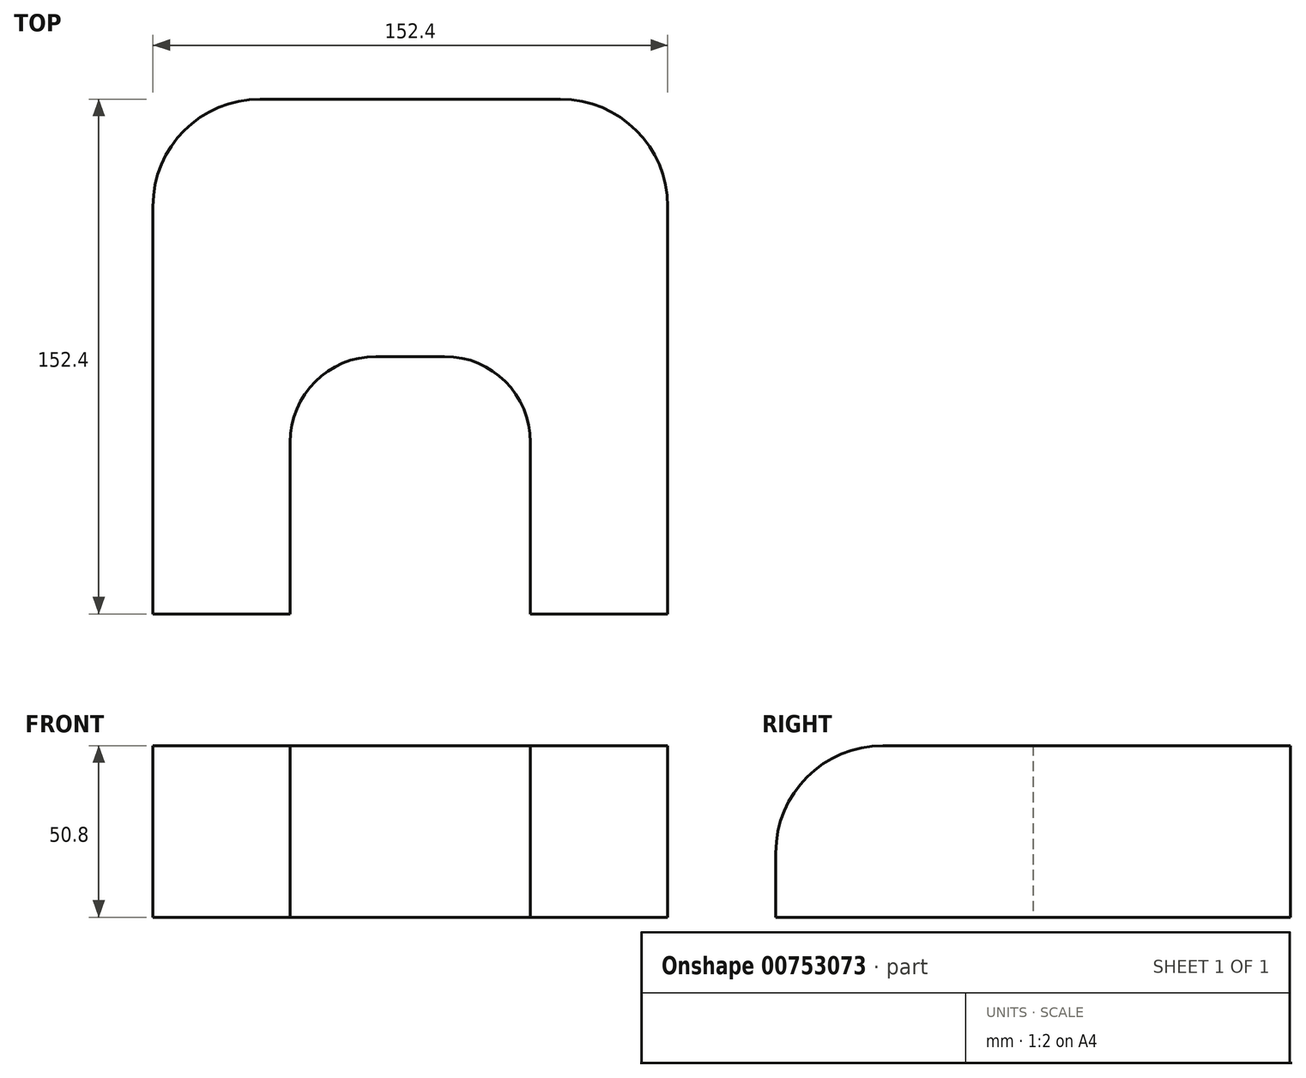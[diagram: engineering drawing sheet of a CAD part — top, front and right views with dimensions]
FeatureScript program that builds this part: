
annotation { "Feature Type Name" : "Feature", "Feature Type Description" : "" }
export const myFeature = defineFeature(function(context is Context, id is Id, definition is map)
    precondition{}
    {
        {
            var Q0;
            Q0=qCreatedBy(makeId("Top.planeOp"),FACE);
            var sketch = newSketch(context, id + "F0", { "sketchPlane" : qUnion([Q0])});
            skLineSegment(sketch, "E0.bottom", {"start": v(0, 0) * mm, "end": v(152.4, 0) * mm});
            skLineSegment(sketch, "E0.top", {"start": v(0, 76.2) * mm, "end": v(152.4, 76.2) * mm});
            skLineSegment(sketch, "E0.left", {"start": v(0, 0) * mm, "end": v(0, 76.2) * mm});
            skLineSegment(sketch, "E0.right", {"start": v(152.4, 0) * mm, "end": v(152.4, 76.2) * mm});
            skLineSegment(sketch, "E1.bottom", {"start": v(0, 0) * mm, "end": v(40.64, 0) * mm});
            skLineSegment(sketch, "E1.top", {"start": v(0, -76.2) * mm, "end": v(40.64, -76.2) * mm});
            skLineSegment(sketch, "E1.left", {"start": v(0, 0) * mm, "end": v(0, -76.2) * mm});
            skLineSegment(sketch, "E1.right", {"start": v(40.64, 0) * mm, "end": v(40.64, -76.2) * mm});
            skLineSegment(sketch, "E2.bottom", {"start": v(152.4, 0) * mm, "end": v(111.76, 0) * mm});
            skLineSegment(sketch, "E2.top", {"start": v(152.4, -76.2) * mm, "end": v(111.76, -76.2) * mm});
            skLineSegment(sketch, "E2.left", {"start": v(152.4, 0) * mm, "end": v(152.4, -76.2) * mm});
            skLineSegment(sketch, "E2.right", {"start": v(111.76, 0) * mm, "end": v(111.76, -76.2) * mm});
            skSolve(sketch);
        }
        {
            var Q0;
            Q0=makeQuery(id+"F0.imprint","IMPRINT",FACE,{"disambiguationData":[TD([[makeQuery(id+"F0.imprint","IMPRINT",EDGE,{"derivedFrom":sQuery(id+"F0.wireOp",EDGE,"E0.top")}),-1.0]])]});
            var Q1;
            Q1=makeQuery(id+"F0.imprint","IMPRINT",FACE,{"disambiguationData":[TD([[makeQuery(id+"F0.imprint","IMPRINT",EDGE,{"derivedFrom":sQuery(id+"F0.wireOp",EDGE,"E1.top")}),1.0]])]});
            var Q2;
            Q2=makeQuery(id+"F0.imprint","IMPRINT",FACE,{"disambiguationData":[TD([[makeQuery(id+"F0.imprint","IMPRINT",EDGE,{"derivedFrom":sQuery(id+"F0.wireOp",EDGE,"E2.top")}),-1.0]])]});
            extrude(context, id + "F1", {"entities" : qUnion([Q0, Q1, Q2]), "depth" : 50.8 * mm, "offsetDistance" : 25.4 * mm});
        }
        {
            var Q0;
            Q0=makeQuery(id+"F1.opExtrude","CAP_EDGE",EDGE,{"disambiguationData":[OSD([sQuery(id+"F0.wireOp",EDGE,"E1.top")])],"isStart":false});
            var Q1;
            Q1=makeQuery(id+"F1.opExtrude","CAP_EDGE",EDGE,{"disambiguationData":[OSD([sQuery(id+"F0.wireOp",EDGE,"E2.top")])],"isStart":false});
            fillet(context, id + "F2", {"entities" : qUnion([Q0, Q1]), "radius" : 31.75 * mm, "tangentPropagation" : true, "allowEdgeOverflow" : false});
        }
        {
            var Q0;
            Q0=makeQuery(id+"F1.opExtrude","SWEPT_EDGE",EDGE,{"disambiguationData":[OSD([sQuery(id+"F0.wireOp",EDGE,"E0.top"),sQuery(id+"F0.wireOp",EDGE,"E0.right")])]});
            var Q1;
            Q1=makeQuery(id+"F1.opExtrude","SWEPT_EDGE",EDGE,{"disambiguationData":[OSD([sQuery(id+"F0.wireOp",EDGE,"E0.top"),sQuery(id+"F0.wireOp",EDGE,"E0.left")])]});
            fillet(context, id + "F3", {"entities" : qUnion([Q0, Q1]), "radius" : 31.75 * mm, "tangentPropagation" : true, "allowEdgeOverflow" : false});
        }
        {
            var Q0;
            Q0=makeQuery(id+"F1.opExtrude","SWEPT_EDGE",EDGE,{"disambiguationData":[OSD([sQuery(id+"F0.wireOp",EDGE,"E0.bottom"),sQuery(id+"F0.wireOp",EDGE,"E2.right")])]});
            var Q1;
            Q1=makeQuery(id+"F1.opExtrude","SWEPT_EDGE",EDGE,{"disambiguationData":[OSD([sQuery(id+"F0.wireOp",EDGE,"E0.bottom"),sQuery(id+"F0.wireOp",EDGE,"E1.right")])]});
            fillet(context, id + "F4", {"entities" : qUnion([Q0, Q1]), "radius" : 25.4 * mm, "tangentPropagation" : true, "allowEdgeOverflow" : false});
        }
    });
